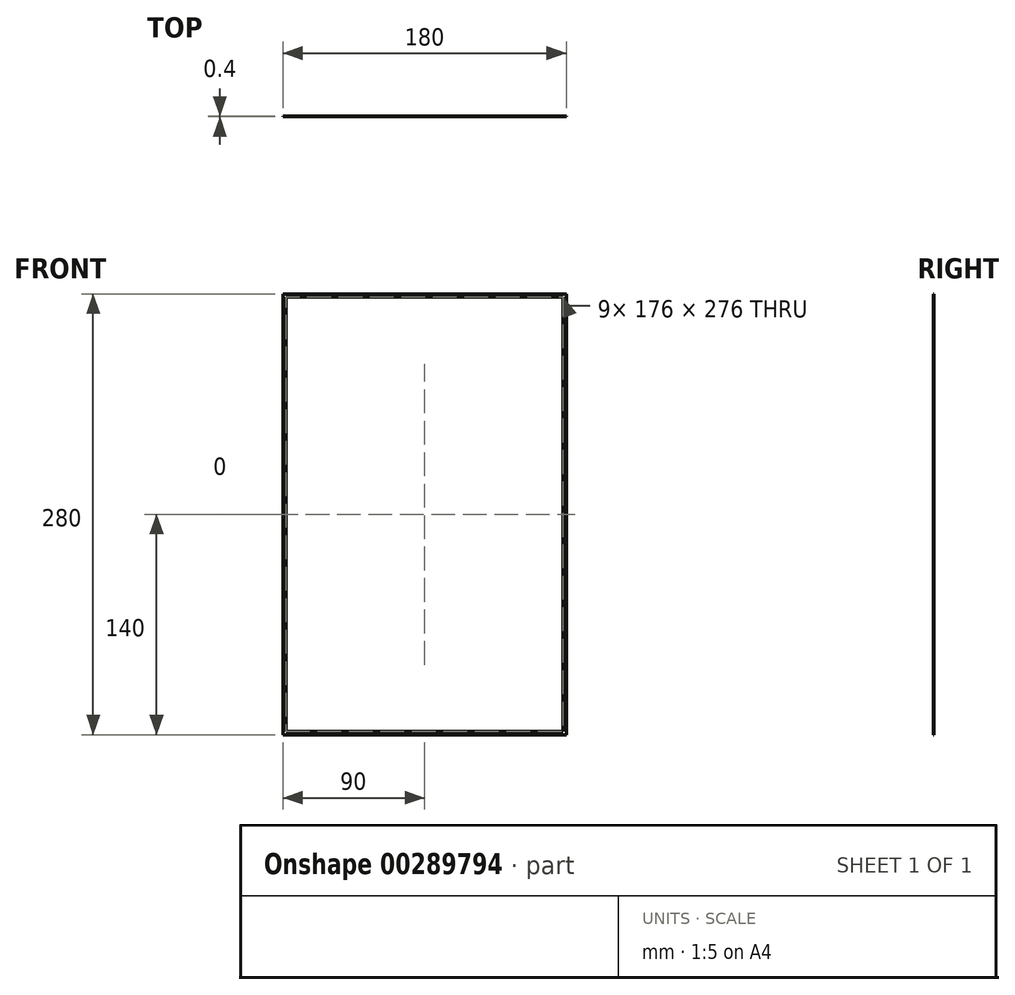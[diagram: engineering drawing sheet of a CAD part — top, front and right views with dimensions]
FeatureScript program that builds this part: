
annotation { "Feature Type Name" : "Feature", "Feature Type Description" : "" }
export const myFeature = defineFeature(function(context is Context, id is Id, definition is map)
    precondition{}
    {
        {
            var Q0;
            Q0=qCreatedBy(makeId("Front.planeOp"),FACE);
            var sketch = newSketch(context, id + "F0", { "sketchPlane" : qUnion([Q0])});
            skLineSegment(sketch, "E0.bottom", {"start": v(90, 140) * mm, "end": v(-90, 140) * mm});
            skLineSegment(sketch, "E0.top", {"start": v(90, -140) * mm, "end": v(-90, -140) * mm});
            skLineSegment(sketch, "E0.left", {"start": v(90, 140) * mm, "end": v(90, -140) * mm});
            skLineSegment(sketch, "E0.right", {"start": v(-90, 140) * mm, "end": v(-90, -140) * mm});
            skPoint(sketch, "E0.middle", {"position": v(0, 0) * mm});
            skLineSegment(sketch, "E1.0", {"start": v(88, 138) * mm, "end": v(88, -138) * mm});
            skLineSegment(sketch, "E1.1", {"start": v(88, 138) * mm, "end": v(-88, 138) * mm});
            skLineSegment(sketch, "E1.2", {"start": v(-88, 138) * mm, "end": v(-88, -138) * mm});
            skLineSegment(sketch, "E1.3", {"start": v(88, -138) * mm, "end": v(-88, -138) * mm});
            skSolve(sketch);
        }
        {
            var Q0;
            Q0 = qSketchRegion(id + "F0", true);
            extrude(context, id + "F1", {"entities" : qUnion([Q0]), "depth" : .4 * mm});
        }
    });
